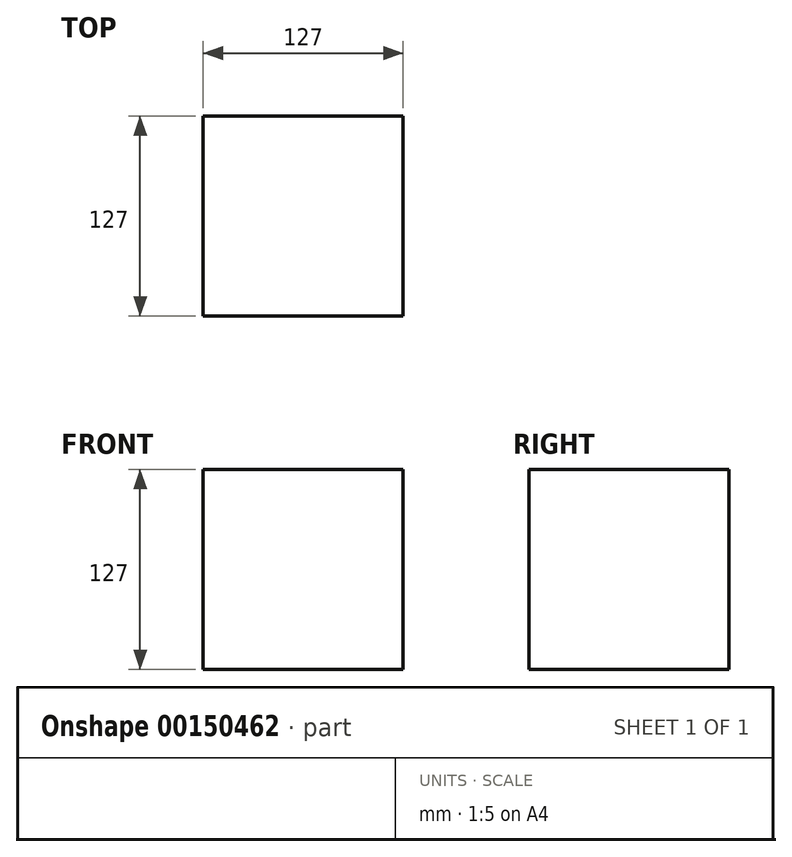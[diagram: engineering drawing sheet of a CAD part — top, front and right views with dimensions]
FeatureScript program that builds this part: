
annotation { "Feature Type Name" : "Feature", "Feature Type Description" : "" }
export const myFeature = defineFeature(function(context is Context, id is Id, definition is map)
    precondition{}
    {
        {
            var Q0;
            Q0=qCreatedBy(makeId("Front.planeOp"),FACE);
            var sketch = newSketch(context, id + "F0", { "sketchPlane" : qUnion([Q0])});
            skPoint(sketch, "E0.start.orphan", {"position": v(0, 99.25) * mm});
            skLineSegment(sketch, "E1", {"start": v(0, 0) * mm, "end": v(127, 0) * mm});
            skLineSegment(sketch, "E2", {"start": v(127, 0) * mm, "end": v(127, 127) * mm});
            skLineSegment(sketch, "E3", {"start": v(127, 127) * mm, "end": v(0, 127) * mm});
            skLineSegment(sketch, "E4", {"start": v(0, 127) * mm, "end": v(0, 0) * mm});
            skSolve(sketch);
        }
        {
            var Q0;
            Q0=makeQuery(id+"F0.imprint","IMPRINT",FACE,{"disambiguationData":[TD([[makeQuery(id+"F0.imprint","IMPRINT",EDGE,{"derivedFrom":sQuery(id+"F0.wireOp",EDGE,"E1")}),1.0]])]});
            extrude(context, id + "F1", {"entities" : qUnion([Q0]), "depth" : 127 * mm});
        }
    });
